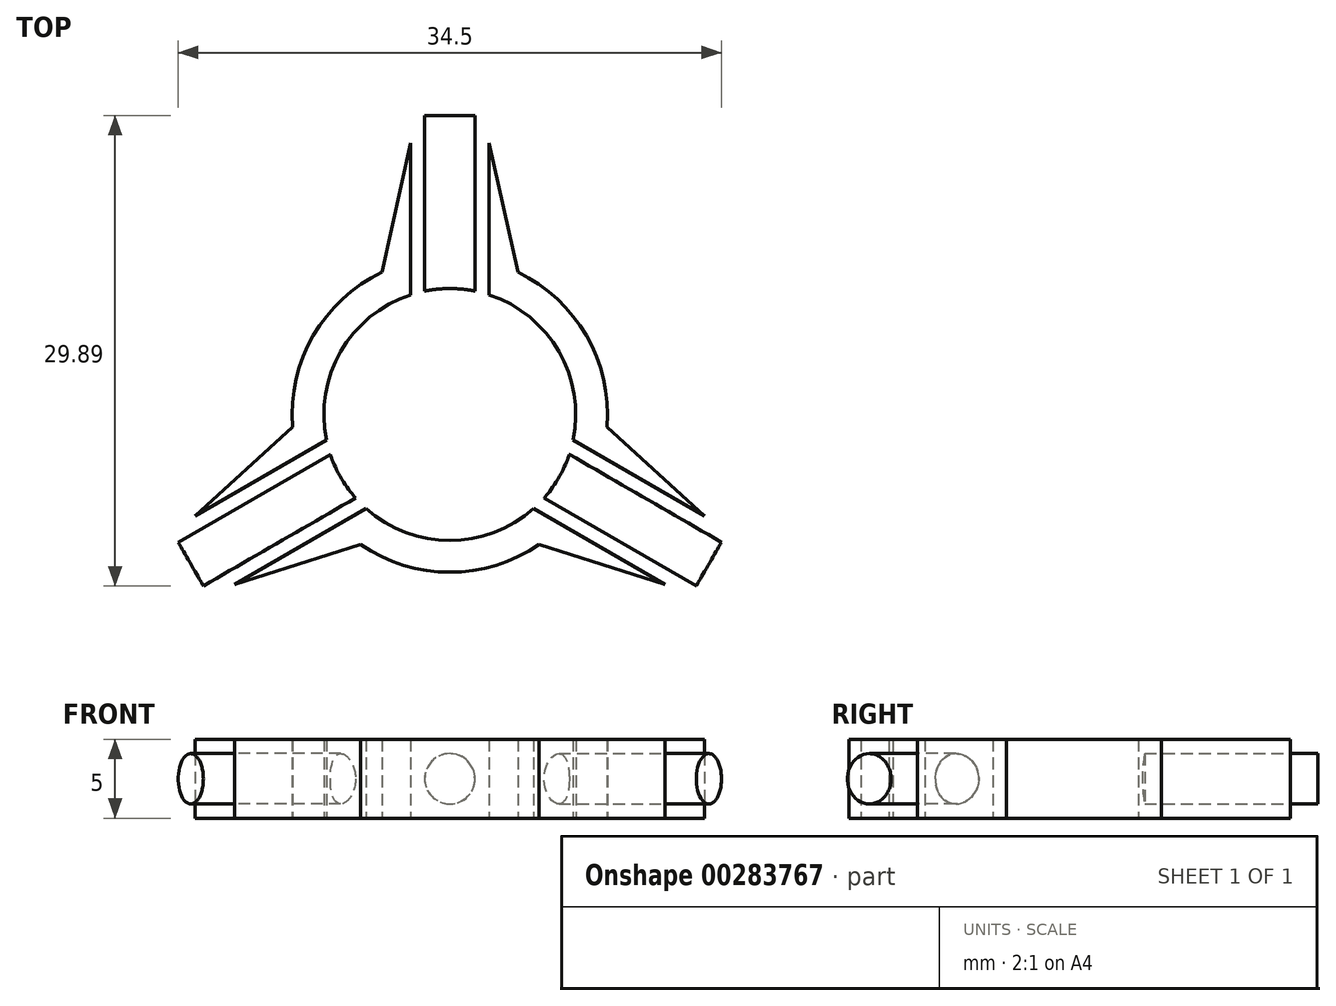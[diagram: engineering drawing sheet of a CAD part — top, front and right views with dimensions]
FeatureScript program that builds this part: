
annotation { "Feature Type Name" : "Feature", "Feature Type Description" : "" }
export const myFeature = defineFeature(function(context is Context, id is Id, definition is map)
    precondition{}
    {
        {
            var Q0;
            Q0=qCreatedBy(makeId("Top.planeOp"),FACE);
            var sketch = newSketch(context, id + "F0", { "sketchPlane" : qUnion([Q0])});
            skCircle(sketch, "E0", {"center": v(0, 0) * mm, "radius": 8 * mm});
            skLineSegment(sketch, "E1.bottom", {"start": v(2.5, 19) * mm, "end": v(-2.5, 19) * mm});
            skLineSegment(sketch, "E1.left", {"start": v(2.5, 19) * mm, "end": v(2.5, 17.24) * mm});
            skLineSegment(sketch, "E1.right", {"start": v(-2.5, 19) * mm, "end": v(-2.5, 17.24) * mm});
            skPoint(sketch, "E1.middle", {"position": v(0, 11) * mm});
            skPoint(sketch, "E1.top.end.orphan", {"position": v(-2.5, 3) * mm});
            skPoint(sketch, "E1.top.start.orphan", {"position": v(2.5, 3) * mm});
            skPoint(sketch, "E2.2.2", {"position": v(0, -11) * mm});
            skLineSegment(sketch, "E3.1.0", {"start": v(-17.7, -7.33) * mm, "end": v(-15.2, -11.67) * mm});
            skPoint(sketch, "E3.1.3", {"position": v(-9.53, -5.5) * mm});
            skLineSegment(sketch, "E3.1.4", {"start": v(-17.7, -7.33) * mm, "end": v(-16.18, -6.46) * mm});
            skLineSegment(sketch, "E3.1.5", {"start": v(-15.2, -11.67) * mm, "end": v(-13.68, -10.79) * mm});
            skLineSegment(sketch, "E3.2.0", {"start": v(15.2, -11.67) * mm, "end": v(17.7, -7.33) * mm});
            skPoint(sketch, "E3.2.3", {"position": v(9.53, -5.5) * mm});
            skLineSegment(sketch, "E3.2.4", {"start": v(15.2, -11.67) * mm, "end": v(13.68, -10.79) * mm});
            skLineSegment(sketch, "E3.2.5", {"start": v(17.7, -7.33) * mm, "end": v(16.18, -6.46) * mm});
            skArc(sketch, "E4", {"start": v(-4.32, 9.04) * mm, "mid": v(-8.68, 5) * mm, "end": v(-9.99, -0.78) * mm});
            skArc(sketch, "E5.trimOffspring", {"start": v(-5.67, -8.26) * mm, "mid": v(0, -10.02) * mm, "end": v(5.67, -8.26) * mm});
            skArc(sketch, "E6.trimOffspring", {"start": v(9.99, -0.78) * mm, "mid": v(8.68, 5) * mm, "end": v(4.32, 9.04) * mm});
            skLineSegment(sketch, "E7", {"start": v(-2.5, 17.24) * mm, "end": v(-4.32, 9.04) * mm});
            skPoint(sketch, "E7.endSnap0", {"position": v(-4.52, 12.42) * mm});
            skLineSegment(sketch, "E8", {"start": v(2.5, 17.24) * mm, "end": v(4.32, 9.04) * mm});
            skPoint(sketch, "E9.orphan", {"position": v(-4.52, 8.15) * mm});
            skPoint(sketch, "E10.orphan", {"position": v(4.52, 8.15) * mm});
            skLineSegment(sketch, "E11.1.0", {"start": v(-13.68, -10.79) * mm, "end": v(-5.67, -8.26) * mm});
            skLineSegment(sketch, "E11.1.1", {"start": v(-16.18, -6.46) * mm, "end": v(-9.99, -0.78) * mm});
            skLineSegment(sketch, "E11.2.0", {"start": v(16.18, -6.46) * mm, "end": v(9.99, -0.78) * mm});
            skLineSegment(sketch, "E11.2.1", {"start": v(13.68, -10.79) * mm, "end": v(5.67, -8.26) * mm});
            skSolve(sketch);
        }
        {
            var Q0;
            Q0=makeQuery(id+"F0.imprint","IMPRINT",FACE,{"disambiguationData":[TD([[makeQuery(id+"F0.imprint","IMPRINT",EDGE,{"derivedFrom":sQuery(id+"F0.wireOp",EDGE,"E0")}),-1.0]])]});
            extrude(context, id + "F1", {"entities" : qUnion([Q0]), "depth" : 5 * mm});
        }
        {
            var Q0;
            Q0=makeQuery(id+"F1.opExtrude","SWEPT_FACE",FACE,{"disambiguationData":[OSD([sQuery(id+"F0.wireOp",EDGE,"E3.2.0")])]});
            var sketch = newSketch(context, id + "F2", { "sketchPlane" : qUnion([Q0])});
            skLineSegment(sketch, "E12", {"start": v(2.5, 5) * mm, "end": v(-2.5, 0) * mm});
            skCircle(sketch, "E13", {"center": v(0, 2.5) * mm, "radius": 1.6 * mm});
            skSolve(sketch);
        }
        {
            var Q0;
            {var subQ0=sQuery(id+"F2.wireOp",EDGE,"E13");var subQ1=sQuery(id+"F2.wireOp",EDGE,"E12");var subQ2=makeQuery(id+"F2.imprint","INTERSECT",VERTEX,{"disambiguationData":[OD(0.0)],"derivedFrom":[subQ1,subQ0]});Q0=makeQuery(id+"F2.imprint","IMPRINT",FACE,{"disambiguationData":[TD([[makeQuery(id+"F2.imprint","IMPRINT",EDGE,{"disambiguationData":[TD([[subQ2,-1.0]])],"derivedFrom":subQ1}),1.0]])]});}
            var Q1;
            {var subQ0=sQuery(id+"F2.wireOp",EDGE,"E13");var subQ1=sQuery(id+"F2.wireOp",EDGE,"E12");var subQ2=makeQuery(id+"F2.imprint","INTERSECT",VERTEX,{"disambiguationData":[OD(0.0)],"derivedFrom":[subQ1,subQ0]});Q1=makeQuery(id+"F2.imprint","IMPRINT",FACE,{"disambiguationData":[TD([[makeQuery(id+"F2.imprint","IMPRINT",EDGE,{"disambiguationData":[TD([[subQ2,-1.0]])],"derivedFrom":subQ1}),-1.0]])]});}
            extrude(context, id + "F3", {"entities" : qUnion([Q0, Q1]), "operationType" : NewBodyOperationType.REMOVE, "oppositeDirection" : true, "depth" : 15 * mm});
        }
        {
            var Q0;
            Q0=makeQuery(id+"F1.opExtrude","SWEPT_FACE",FACE,{"disambiguationData":[OSD([sQuery(id+"F0.wireOp",EDGE,"E1.bottom")])]});
            var sketch = newSketch(context, id + "F4", { "sketchPlane" : qUnion([Q0])});
            skLineSegment(sketch, "E14", {"start": v(2.5, 0) * mm, "end": v(-2.5, 5) * mm});
            skCircle(sketch, "E15", {"center": v(0, 2.5) * mm, "radius": 1.6 * mm});
            skSolve(sketch);
        }
        {
            var Q0;
            {var subQ0=sQuery(id+"F4.wireOp",EDGE,"E15");var subQ1=sQuery(id+"F4.wireOp",EDGE,"E14");var subQ2=makeQuery(id+"F4.imprint","INTERSECT",VERTEX,{"disambiguationData":[OD(0.0)],"derivedFrom":[subQ1,subQ0]});Q0=makeQuery(id+"F4.imprint","IMPRINT",FACE,{"disambiguationData":[TD([[makeQuery(id+"F4.imprint","IMPRINT",EDGE,{"disambiguationData":[TD([[subQ2,-1.0]])],"derivedFrom":subQ1}),-1.0]])]});}
            var Q1;
            {var subQ0=sQuery(id+"F4.wireOp",EDGE,"E15");var subQ1=sQuery(id+"F4.wireOp",EDGE,"E14");var subQ2=makeQuery(id+"F4.imprint","INTERSECT",VERTEX,{"disambiguationData":[OD(0.0)],"derivedFrom":[subQ1,subQ0]});Q1=makeQuery(id+"F4.imprint","IMPRINT",FACE,{"disambiguationData":[TD([[makeQuery(id+"F4.imprint","IMPRINT",EDGE,{"disambiguationData":[TD([[subQ2,-1.0]])],"derivedFrom":subQ1}),1.0]])]});}
            extrude(context, id + "F5", {"entities" : qUnion([Q0, Q1]), "operationType" : NewBodyOperationType.REMOVE, "oppositeDirection" : true, "depth" : 15 * mm});
        }
        {
            var Q0;
            Q0=makeQuery(id+"F1.opExtrude","SWEPT_FACE",FACE,{"disambiguationData":[OSD([sQuery(id+"F0.wireOp",EDGE,"E3.1.0")])]});
            var sketch = newSketch(context, id + "F6", { "sketchPlane" : qUnion([Q0])});
            skLineSegment(sketch, "E16", {"start": v(-2.5, 0) * mm, "end": v(2.5, 5) * mm});
            skCircle(sketch, "E17", {"center": v(0, 2.5) * mm, "radius": 1.6 * mm});
            skSolve(sketch);
        }
        {
            var Q0;
            {var subQ0=sQuery(id+"F6.wireOp",EDGE,"E17");var subQ1=sQuery(id+"F6.wireOp",EDGE,"E16");var subQ2=makeQuery(id+"F6.imprint","INTERSECT",VERTEX,{"disambiguationData":[OD(0.0)],"derivedFrom":[subQ1,subQ0]});Q0=makeQuery(id+"F6.imprint","IMPRINT",FACE,{"disambiguationData":[TD([[makeQuery(id+"F6.imprint","IMPRINT",EDGE,{"disambiguationData":[TD([[subQ2,-1.0]])],"derivedFrom":subQ1}),1.0]])]});}
            var Q1;
            {var subQ0=sQuery(id+"F6.wireOp",EDGE,"E17");var subQ1=sQuery(id+"F6.wireOp",EDGE,"E16");var subQ2=makeQuery(id+"F6.imprint","INTERSECT",VERTEX,{"disambiguationData":[OD(0.0)],"derivedFrom":[subQ1,subQ0]});Q1=makeQuery(id+"F6.imprint","IMPRINT",FACE,{"disambiguationData":[TD([[makeQuery(id+"F6.imprint","IMPRINT",EDGE,{"disambiguationData":[TD([[subQ2,-1.0]])],"derivedFrom":subQ1}),-1.0]])]});}
            extrude(context, id + "F7", {"entities" : qUnion([Q0, Q1]), "operationType" : NewBodyOperationType.REMOVE, "oppositeDirection" : true, "depth" : 15 * mm});
        }
    });
